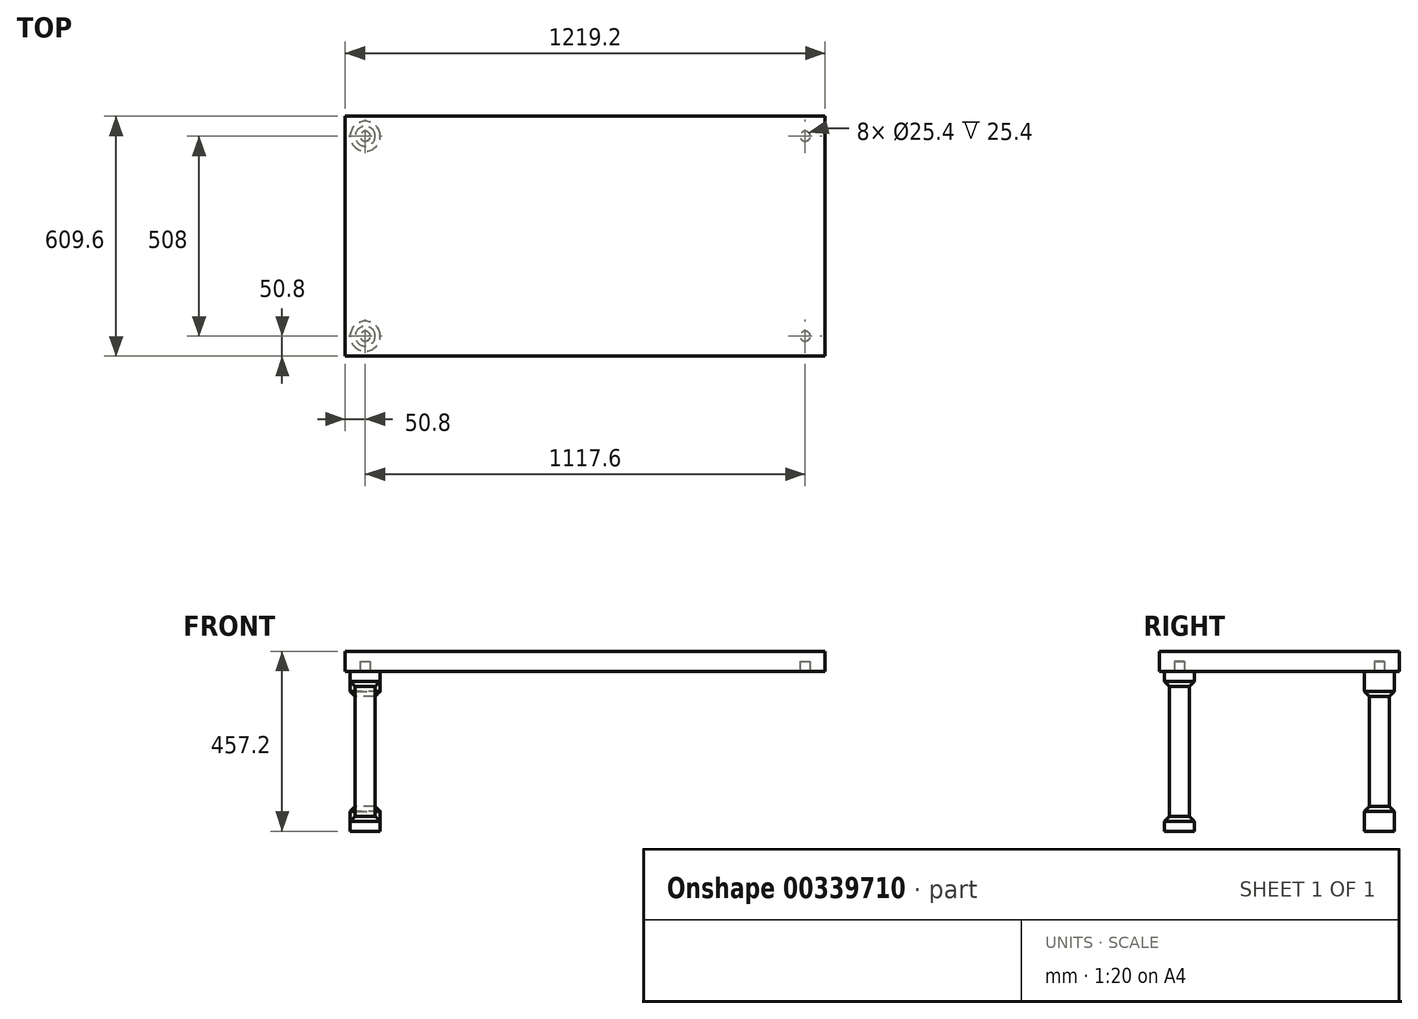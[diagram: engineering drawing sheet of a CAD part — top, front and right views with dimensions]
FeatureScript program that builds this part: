
annotation { "Feature Type Name" : "Feature", "Feature Type Description" : "" }
export const myFeature = defineFeature(function(context is Context, id is Id, definition is map)
    precondition{}
    {
        {
            var Q0;
            Q0=qCreatedBy(makeId("Top.planeOp"),FACE);
            var sketch = newSketch(context, id + "F0", { "sketchPlane" : qUnion([Q0])});
            skLineSegment(sketch, "E0.bottom", {"start": v(609.6, -304.8) * mm, "end": v(-609.6, -304.8) * mm});
            skLineSegment(sketch, "E0.top", {"start": v(609.6, 304.8) * mm, "end": v(-609.6, 304.8) * mm});
            skLineSegment(sketch, "E0.left", {"start": v(609.6, -304.8) * mm, "end": v(609.6, 304.8) * mm});
            skLineSegment(sketch, "E0.right", {"start": v(-609.6, -304.8) * mm, "end": v(-609.6, 304.8) * mm});
            skPoint(sketch, "E0.middle", {"position": v(0, 0) * mm});
            skSolve(sketch);
        }
        {
            var Q0;
            Q0=qCreatedBy(makeId("Top.planeOp"),FACE);
            var sketch = newSketch(context, id + "F1", { "sketchPlane" : qUnion([Q0])});
            skLineSegment(sketch, "E1.bottom", {"start": v(609.6, -304.8) * mm, "end": v(-609.6, -304.8) * mm});
            skLineSegment(sketch, "E1.top", {"start": v(609.6, 304.8) * mm, "end": v(-609.6, 304.8) * mm});
            skLineSegment(sketch, "E1.left", {"start": v(609.6, -304.8) * mm, "end": v(609.6, 304.8) * mm});
            skLineSegment(sketch, "E1.right", {"start": v(-609.6, -304.8) * mm, "end": v(-609.6, 304.8) * mm});
            skPoint(sketch, "E1.middle", {"position": v(0, 0) * mm});
            skSolve(sketch);
        }
        {
            var Q0;
            Q0=makeQuery(id+"F0.imprint","IMPRINT",FACE,{"disambiguationData":[TD([[makeQuery(id+"F0.imprint","IMPRINT",EDGE,{"derivedFrom":sQuery(id+"F0.wireOp",EDGE,"E0.bottom")}),-1.0]])]});
            var Q1;
            Q1=sQuery(id+"F0.wireOp",EDGE,"E0.right");
            extrude(context, id + "F2", {"entities" : qUnion([Q0]), "surfaceEntities" : qUnion([Q1]), "oppositeDirection" : true, "depth" : 50.8 * mm, "symmetric" : true});
        }
        {
            var Q0;
            Q0 = qSketchRegion(id + "F1", true);
            extrude(context, id + "F3", {"entities" : qUnion([Q0]), "depth" : 50.8 * mm, "symmetric" : true});
        }
        {
            var Q0;
            Q0=makeQuery(id+"F3.opExtrude","CAP_FACE",FACE,{"disambiguationData":[OSD([sQuery(id+"F1.wireOp",EDGE,"E1.bottom"),sQuery(id+"F1.wireOp",EDGE,"E1.top"),sQuery(id+"F1.wireOp",EDGE,"E1.left"),sQuery(id+"F1.wireOp",EDGE,"E1.right")])],"isStart":true});
            var sketch = newSketch(context, id + "F4", { "sketchPlane" : qUnion([Q0])});
            skLineSegment(sketch, "E2.bottom", {"start": v(-609.6, 304.8) * mm, "end": v(-558.8, 304.8) * mm, "construction": true});
            skLineSegment(sketch, "E2.top", {"start": v(-609.6, 254) * mm, "end": v(-558.8, 254) * mm, "construction": true});
            skLineSegment(sketch, "E2.left", {"start": v(-609.6, 304.8) * mm, "end": v(-609.6, 254) * mm, "construction": true});
            skLineSegment(sketch, "E2.right", {"start": v(-558.8, 304.8) * mm, "end": v(-558.8, 254) * mm, "construction": true});
            skLineSegment(sketch, "E3.bottom", {"start": v(-609.6, -304.8) * mm, "end": v(-558.8, -304.8) * mm, "construction": true});
            skLineSegment(sketch, "E3.top", {"start": v(-609.6, -254) * mm, "end": v(-558.8, -254) * mm, "construction": true});
            skLineSegment(sketch, "E3.left", {"start": v(-609.6, -304.8) * mm, "end": v(-609.6, -254) * mm, "construction": true});
            skLineSegment(sketch, "E3.right", {"start": v(-558.8, -304.8) * mm, "end": v(-558.8, -254) * mm, "construction": true});
            skLineSegment(sketch, "E4.bottom", {"start": v(609.6, -304.8) * mm, "end": v(558.8, -304.8) * mm, "construction": true});
            skLineSegment(sketch, "E4.top", {"start": v(609.6, -254) * mm, "end": v(558.8, -254) * mm, "construction": true});
            skLineSegment(sketch, "E4.left", {"start": v(609.6, -304.8) * mm, "end": v(609.6, -254) * mm, "construction": true});
            skLineSegment(sketch, "E4.right", {"start": v(558.8, -304.8) * mm, "end": v(558.8, -254) * mm, "construction": true});
            skLineSegment(sketch, "E5.bottom", {"start": v(609.6, 304.8) * mm, "end": v(558.8, 304.8) * mm, "construction": true});
            skLineSegment(sketch, "E5.top", {"start": v(609.6, 254) * mm, "end": v(558.8, 254) * mm, "construction": true});
            skLineSegment(sketch, "E5.left", {"start": v(609.6, 304.8) * mm, "end": v(609.6, 254) * mm, "construction": true});
            skLineSegment(sketch, "E5.right", {"start": v(558.8, 304.8) * mm, "end": v(558.8, 254) * mm, "construction": true});
            skCircle(sketch, "E6", {"center": v(-558.8, 254) * mm, "radius": 12.7 * mm});
            skCircle(sketch, "E7", {"center": v(-558.8, -254) * mm, "radius": 12.7 * mm});
            skCircle(sketch, "E8", {"center": v(558.8, -254) * mm, "radius": 12.7 * mm});
            skCircle(sketch, "E9", {"center": v(558.8, 254) * mm, "radius": 12.7 * mm});
            skSolve(sketch);
        }
        {
            var Q0;
            Q0=qCreatedBy(makeId("Front.planeOp"),FACE);
            var Q1;
            Q1=sQuery(id+"F4.wireOp",VERTEX,"E6.center");
            cPlane(context, id + "F5", {"entities" : qUnion([Q0, Q1]), "cplaneType" : CPlaneType.PLANE_POINT, "offset" : 25.4 * mm, "width" : 152.4 * mm, "height" : 152.4 * mm});
        }
        {
            var Q0;
            Q0=qCreatedBy(id+"F5.planeOp",FACE);
            var sketch = newSketch(context, id + "F6", { "sketchPlane" : qUnion([Q0])});
            skLineSegment(sketch, "E10.0", {"start": v(-546.1, -25.4) * mm, "end": v(-571.5, -25.4) * mm, "construction": true});
            skLineSegment(sketch, "E11", {"start": v(-571.5, -25.4) * mm, "end": v(-571.5, 0) * mm});
            skLineSegment(sketch, "E12", {"start": v(-571.5, 0) * mm, "end": v(-558.8, 0) * mm});
            skPoint(sketch, "E12.endSnap0", {"position": v(-558.8, -25.4) * mm});
            skLineSegment(sketch, "E13", {"start": v(-558.8, 0) * mm, "end": v(-558.8, -431.8) * mm});
            skLineSegment(sketch, "E14", {"start": v(-558.8, -431.8) * mm, "end": v(-596.9, -431.8) * mm});
            skLineSegment(sketch, "E15", {"start": v(-596.9, -431.8) * mm, "end": v(-596.9, -406.4) * mm});
            skLineSegment(sketch, "E16", {"start": v(-596.9, -406.4) * mm, "end": v(-584.2, -393.7) * mm});
            skLineSegment(sketch, "E17", {"start": v(-584.2, -393.7) * mm, "end": v(-584.2, -63.5) * mm});
            skLineSegment(sketch, "E18", {"start": v(-584.2, -63.5) * mm, "end": v(-596.9, -50.8) * mm});
            skLineSegment(sketch, "E19", {"start": v(-596.9, -50.8) * mm, "end": v(-596.9, -25.4) * mm});
            skLineSegment(sketch, "E20", {"start": v(-596.9, -25.4) * mm, "end": v(-571.5, -25.4) * mm});
            skSolve(sketch);
        }
        {
            var Q0;
            Q0 = qSketchRegion(id + "F6", true);
            var Q1;
            Q1=sQuery(id+"F6.wireOp",EDGE,"E13");
            revolve(context, id + "F7", {"entities" : qUnion([Q0]), "axis" : qUnion([Q1]), "revolveType" : RevolveType.FULL});
        }
        {
            var Q0;
            Q0=makeQuery(id+"F3.opExtrude","SWEPT_FACE",FACE,{"disambiguationData":[OSD([sQuery(id+"F1.wireOp",EDGE,"E1.top")])]});
            var Q1;
            Q1=sQuery(id+"F4.wireOp",VERTEX,"E7.center");
            cPlane(context, id + "F8", {"entities" : qUnion([Q0, Q1]), "cplaneType" : CPlaneType.PLANE_POINT, "offset" : 25.4 * mm, "width" : 152.4 * mm, "height" : 152.4 * mm});
        }
        {
            var Q0;
            Q0=qCreatedBy(id+"F8.planeOp",FACE);
            var sketch = newSketch(context, id + "F9", { "sketchPlane" : qUnion([Q0])});
            skPoint(sketch, "E21.0", {"position": v(558.8, -25.4) * mm});
            skLineSegment(sketch, "E22", {"start": v(558.8, -25.4) * mm, "end": v(558.8, -431.8) * mm});
            skLineSegment(sketch, "E23", {"start": v(558.8, -431.8) * mm, "end": v(596.9, -431.8) * mm});
            skLineSegment(sketch, "E24", {"start": v(596.9, -431.8) * mm, "end": v(596.9, -381) * mm});
            skLineSegment(sketch, "E25", {"start": v(596.9, -381) * mm, "end": v(584.2, -368.3) * mm});
            skLineSegment(sketch, "E26", {"start": v(584.2, -368.3) * mm, "end": v(584.2, -88.9) * mm});
            skLineSegment(sketch, "E27", {"start": v(584.2, -88.9) * mm, "end": v(596.9, -76.2) * mm});
            skLineSegment(sketch, "E28", {"start": v(596.9, -76.2) * mm, "end": v(596.9, -25.4) * mm});
            skLineSegment(sketch, "E29", {"start": v(596.9, -25.4) * mm, "end": v(558.8, -25.4) * mm});
            skSolve(sketch);
        }
        {
            var Q0;
            Q0 = qSketchRegion(id + "F9", true);
            var Q1;
            Q1=sQuery(id+"F9.wireOp",EDGE,"E22");
            revolve(context, id + "F10", {"entities" : qUnion([Q0]), "axis" : qUnion([Q1]), "revolveType" : RevolveType.FULL});
        }
        {
            var Q0;
            Q0 = qSketchRegion(id + "F4", true);
            extrude(context, id + "F11", {"entities" : qUnion([Q0]), "operationType" : NewBodyOperationType.REMOVE, "oppositeDirection" : true, "depth" : 25.4 * mm});
        }
    });
